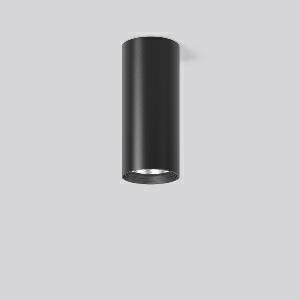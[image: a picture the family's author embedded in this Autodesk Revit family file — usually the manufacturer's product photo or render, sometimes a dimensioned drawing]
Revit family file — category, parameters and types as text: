
# Revit family: heledon_mini_a_931210_003_76_5bef
name_source: partatom
category: Lighting Fixtures
units: mm (PartAtom-declared; Revit-internal decimal feet)

## family parameters
Cut with Voids When Loaded = No
Host = Face
Light Source = No
Part Type = Normal
Room Calculation Point = No
Round Connector Dimension = Use Diameter
Shared = No

## types (1)
- HELEDON mini A (1 x LED Modul 930, 3650 lm, 3000)
    Apparent Load = 29 VA
    Approval mark = CE
    CIE Flux Codes = 95 99 100 100 100
    Color Rendering = 90
    Color Temperature = 3000
    Default Elevation = 1800 mm
    Description = Series: HELEDON mini
Cylindrical surface-mounted downlight. Housing: die-cast aluminium, powder-coated. Internal ceiling frame polycarbonate with bayonet mounting. Black plastic ring and recessed LED to prevent glare from the side. Optical assembly with reflector made of MIRO-Silver with 98% total light reflection for outstanding efficiency - can be changed without tools. Best colour rendering index Ra>90. Suitable for Ceiling mounting. Easy installation with a separate ceiling frame with bayonet mounting and plug connection. Driver integrated. Connected via plug-in connector. High quality converter without flickering and stroboscopic effect. The following accessories can be mounted without use of tools: interchangeable lenses, decorative glasses, honeycomb louvre, clear and frosted diffusers, white interchangeable plastic ring. 
Colour: deep black, matt (RAL 9005)
Diameter: 87 mm
Height: 197 mm
Lamp: LED
Socket: without socket
Colour temperature: 3000K
Colour rendering index (CRI): 92
System power: 29 W
Rated luminous flux: 3650 lm
Luminous efficiency: 126 lm/W
Control gear: Converter, dimmable, DALI
Protection class: I
Type of protection: IP 20
    Height = 197 mm
    Lamp = 1 x LED Modul 930
    Lamp Light Flux = 3650 lm
    Lamp count = 1
    Length = 87 mm
    Lifetime = 50000 h
    Luminous efficacy = 126 lm/W
    Manufacturer = RZB
    ModVariant = No
    Model = 931210.003.76
    Mounting Place = Ceiling
    Mounting Type = Surface mounted
    Number of Poles = 1
    OnlyDefault = Yes
    Power Factor = 1
    Product Name = HELEDON mini A
    Product group = Surface mounted downlights
    ProductGroupID = 302
    Protection Class = Protection class I
    Protection Degree = IP 20
    RLX_Detail_Level = 1
    RLX_Emergency_Light_Flux = 0 lm
    RLX_Emergency_Type = 0
    RLX_Emergency_Type_DB = No
    RlxData = <blob elided: 106321 chars, md5=59d30a99>
    Socket = socket
    Standby Power = 0 W
    System Light Flux = 3650 lm
    System Power = 29 W
    Type Comments = Product without accessories
    Type Image = 931188.003.jpg
    URL = http://relux.com
    VarID = ---
    Voltage = 230 V
    Voltage Range = 220-240 V
    Weight = 0.00 kg
    Width = 0 mm  [stored 0 ft]

note: [stored X ft] marks values corroborated as IEEE doubles in the binary element streams (Revit-internal decimal feet)

## geometry (parser evidence)
native form markers: Blend x4, Sweep x10
no freeform markers — native parametric forms only
